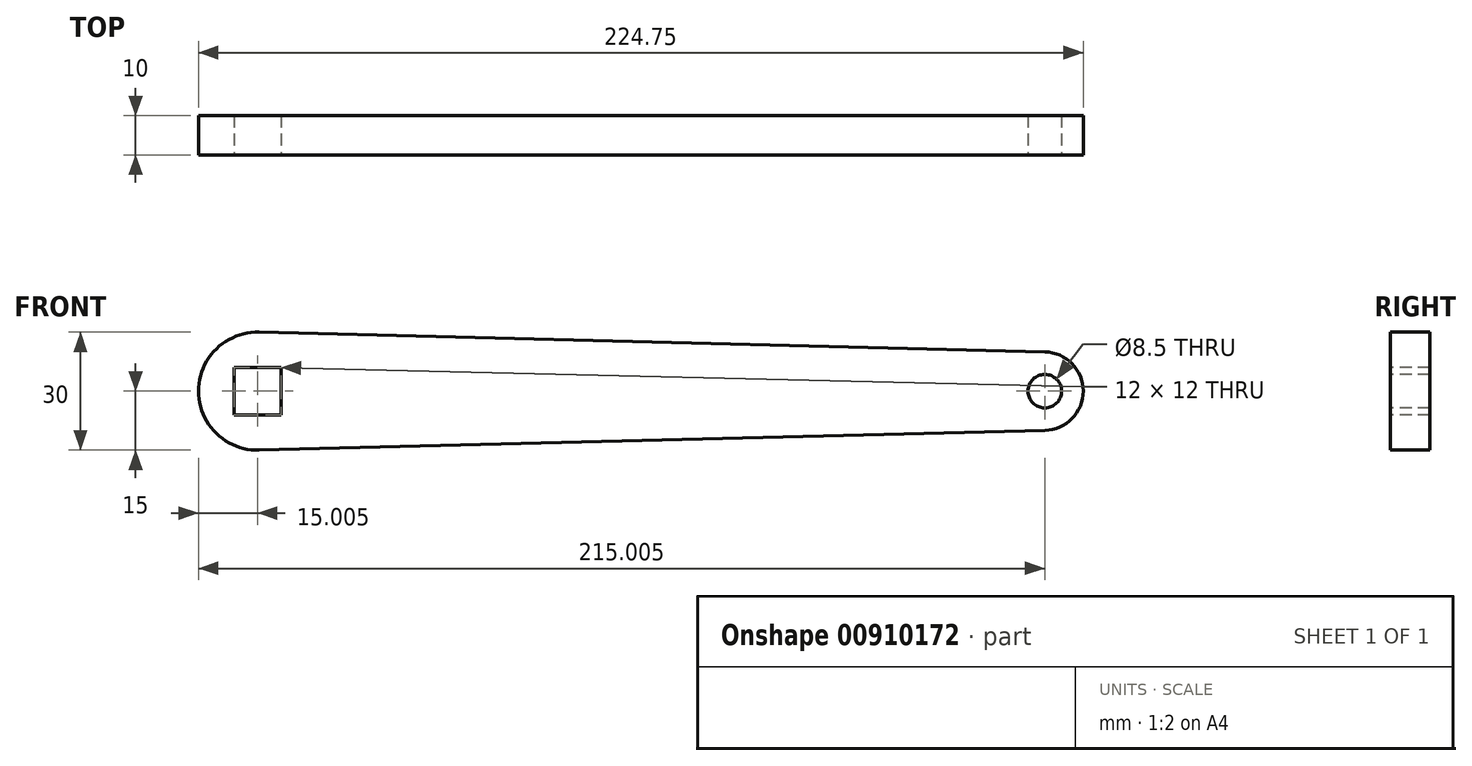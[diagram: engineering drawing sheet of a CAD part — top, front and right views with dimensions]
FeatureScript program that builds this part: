
annotation { "Feature Type Name" : "Feature", "Feature Type Description" : "" }
export const myFeature = defineFeature(function(context is Context, id is Id, definition is map)
    precondition{}
    {
        {
            var Q0;
            Q0=qCreatedBy(makeId("Front.planeOp"),FACE);
            var sketch = newSketch(context, id + "F0", { "sketchPlane" : qUnion([Q0])});
            skPoint(sketch, "E0", {"position": v(199.62, 0) * mm});
            skLineSegment(sketch, "E1", {"start": v(0, 15) * mm, "end": v(199.62, 10) * mm});
            skLineSegment(sketch, "E2.MirrorCS", {"start": v(0, -15) * mm, "end": v(199.62, -10) * mm});
            skArc(sketch, "E3", {"start": v(199.62, 10) * mm, "mid": v(209.37, 0) * mm, "end": v(199.62, -10) * mm});
            skArc(sketch, "E4", {"start": v(0, 15) * mm, "mid": v(-15.38, 0) * mm, "end": v(0, -15) * mm});
            skLineSegment(sketch, "E5.bottom", {"start": v(-6.38, -6) * mm, "end": v(5.62, -6) * mm});
            skLineSegment(sketch, "E5.top", {"start": v(-6.38, 6) * mm, "end": v(5.62, 6) * mm});
            skLineSegment(sketch, "E5.left", {"start": v(-6.38, -6) * mm, "end": v(-6.38, 6) * mm});
            skLineSegment(sketch, "E5.right", {"start": v(5.62, -6) * mm, "end": v(5.62, 6) * mm});
            skSolve(sketch);
        }
        {
            var Q0;
            Q0 = qSketchRegion(id + "F0", true);
            extrude(context, id + "F1", {"entities" : qUnion([Q0]), "oppositeDirection" : true, "depth" : 10 * mm, "offsetDistance" : 25 * mm});
        }
        {
            var Q0;
            Q0=sQuery(id+"F0.wireOp",VERTEX,"E0");
            var Q1;
            Q1=makeQuery(id+"F1.opExtrude","SWEPT_BODY",BODY,{"disambiguationData":[OSD([sQuery(id+"F0.wireOp",EDGE,"E1"),sQuery(id+"F0.wireOp",EDGE,"E2.MirrorCS"),sQuery(id+"F0.wireOp",EDGE,"E3"),sQuery(id+"F0.wireOp",EDGE,"E4"),sQuery(id+"F0.wireOp",EDGE,"E5.bottom"),sQuery(id+"F0.wireOp",EDGE,"E5.top"),sQuery(id+"F0.wireOp",EDGE,"E5.left"),sQuery(id+"F0.wireOp",EDGE,"E5.right")])]});
            hole(context, id + "F2", {"style" : HoleStyle.SIMPLE, "endStyle" : HoleEndStyle.BLIND, "standardTappedOrClearance" : lookupTablePath({ "standard" : "ISO", "engagement" : "75%", "pitch" : "1.5 mm", "size" : "M10", "type" : "Tapped" }), "standardBlindInLast" : lookupTablePath({ "standard" : "ISO", "engagement" : "75%", "pitch" : "1.5 mm", "size" : "M10", "type" : "Tapped" }), "holeDiameter" : 8.5 * mm, "majorDiameter" : 10 * mm, "showTappedDepth" : true, "holeDepth" : 16.5 * mm, "isTappedThrough" : true, "tappedDepth" : 12 * mm, "tapClearance" : 3, "locations" : qUnion([Q0]), "scope" : qUnion([Q1])});
        }
    });
